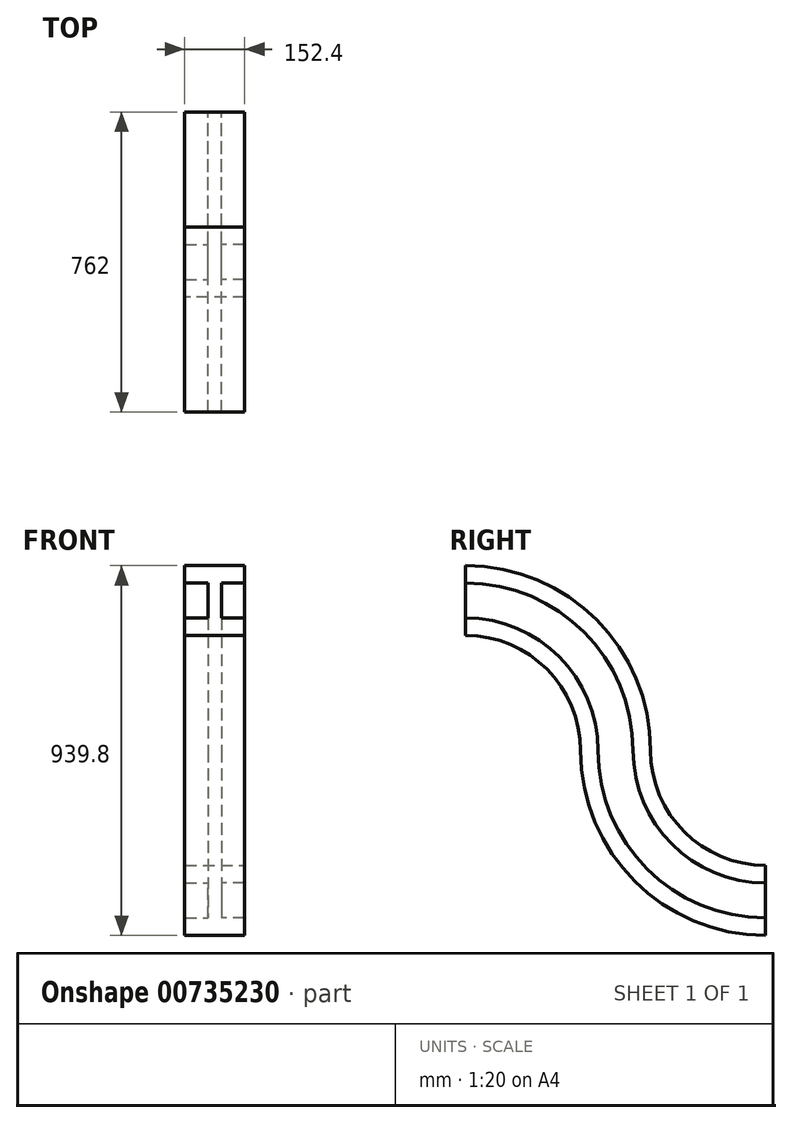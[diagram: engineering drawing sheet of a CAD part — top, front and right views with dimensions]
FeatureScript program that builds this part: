
annotation { "Feature Type Name" : "Feature", "Feature Type Description" : "" }
export const myFeature = defineFeature(function(context is Context, id is Id, definition is map)
    precondition{}
    {
        {
            var Q0;
            Q0=qCreatedBy(makeId("Front.planeOp"),FACE);
            var sketch = newSketch(context, id + "F0", { "sketchPlane" : qUnion([Q0])});
            skLineSegment(sketch, "E0", {"start": v(0, 88.9) * mm, "end": v(76.2, 88.9) * mm});
            skLineSegment(sketch, "E1", {"start": v(76.2, 88.9) * mm, "end": v(76.2, 44.45) * mm});
            skLineSegment(sketch, "E2", {"start": v(76.2, 44.45) * mm, "end": v(17.37, 44.45) * mm});
            skLineSegment(sketch, "E3", {"start": v(0, 88.9) * mm, "end": v(0, -88.9) * mm, "construction": true});
            skLineSegment(sketch, "E4", {"start": v(-17.37, 0) * mm, "end": v(17.37, 0) * mm, "construction": true});
            skLineSegment(sketch, "E5", {"start": v(17.37, 0) * mm, "end": v(17.37, 44.45) * mm});
            skLineSegment(sketch, "E6.MirrorCS", {"start": v(0, 88.9) * mm, "end": v(-76.2, 88.9) * mm});
            skLineSegment(sketch, "E7.MirrorCS", {"start": v(-76.2, 88.9) * mm, "end": v(-76.2, 44.45) * mm});
            skLineSegment(sketch, "E8.MirrorCS", {"start": v(-17.37, 0) * mm, "end": v(-17.37, 44.45) * mm});
            skLineSegment(sketch, "E9.MirrorCS", {"start": v(-76.2, 44.45) * mm, "end": v(-17.37, 44.45) * mm});
            skLineSegment(sketch, "E10.MirrorCS", {"start": v(0, -88.9) * mm, "end": v(-76.2, -88.9) * mm});
            skLineSegment(sketch, "E11.MirrorCS", {"start": v(-76.2, -88.9) * mm, "end": v(-76.2, -44.45) * mm});
            skLineSegment(sketch, "E12.MirrorCS", {"start": v(-76.2, -44.45) * mm, "end": v(-17.37, -44.45) * mm});
            skLineSegment(sketch, "E13.MirrorCS", {"start": v(-17.37, 0) * mm, "end": v(-17.37, -44.45) * mm});
            skLineSegment(sketch, "E14.MirrorCS", {"start": v(76.2, -44.45) * mm, "end": v(17.37, -44.45) * mm});
            skLineSegment(sketch, "E15.MirrorCS", {"start": v(0, -88.9) * mm, "end": v(76.2, -88.9) * mm});
            skLineSegment(sketch, "E16.MirrorCS", {"start": v(17.37, 0) * mm, "end": v(17.37, -44.45) * mm});
            skLineSegment(sketch, "E17.MirrorCS", {"start": v(76.2, -88.9) * mm, "end": v(76.2, -44.45) * mm});
            skSolve(sketch);
        }
        {
            var Q0;
            Q0=qCreatedBy(makeId("Right.planeOp"),FACE);
            var sketch = newSketch(context, id + "F1", { "sketchPlane" : qUnion([Q0])});
            skArc(sketch, "E18", {"start": v(0, 0) * mm, "mid": v(269.4, -111.6) * mm, "end": v(381, -381) * mm});
            skArc(sketch, "E19", {"start": v(381, -381) * mm, "mid": v(492.6, -650.4) * mm, "end": v(762, -762) * mm});
            skSolve(sketch);
        }
        {
            var Q0;
            Q0=makeQuery(id+"F0.imprint","IMPRINT",FACE,{"disambiguationData":[TD([[makeQuery(id+"F0.imprint","IMPRINT",EDGE,{"derivedFrom":sQuery(id+"F0.wireOp",EDGE,"E0")}),-1.0]])]});
            var Q1;
            Q1=sQuery(id+"F1.wireOp",EDGE,"E18");
            sweep(context, id + "F2", {"profiles" : qUnion([Q0]), "path" : qUnion([Q1])});
        }
        {
            var Q0;
            Q0=makeQuery(id+"F2.opSweep","CAP_FACE",FACE,{"disambiguationData":[OSD([sQuery(id+"F0.wireOp",EDGE,"E0"),sQuery(id+"F0.wireOp",EDGE,"E1"),sQuery(id+"F0.wireOp",EDGE,"E2"),sQuery(id+"F0.wireOp",EDGE,"E5"),sQuery(id+"F0.wireOp",EDGE,"E6.MirrorCS"),sQuery(id+"F0.wireOp",EDGE,"E8.MirrorCS"),sQuery(id+"F0.wireOp",EDGE,"E9.MirrorCS"),sQuery(id+"F0.wireOp",EDGE,"E7.MirrorCS"),sQuery(id+"F0.wireOp",EDGE,"E10.MirrorCS"),sQuery(id+"F0.wireOp",EDGE,"E11.MirrorCS"),sQuery(id+"F0.wireOp",EDGE,"E12.MirrorCS"),sQuery(id+"F0.wireOp",EDGE,"E13.MirrorCS"),sQuery(id+"F0.wireOp",EDGE,"E14.MirrorCS"),sQuery(id+"F0.wireOp",EDGE,"E15.MirrorCS"),sQuery(id+"F0.wireOp",EDGE,"E16.MirrorCS"),sQuery(id+"F0.wireOp",EDGE,"E17.MirrorCS"),sQuery(id+"F1.wireOp",VERTEX,"E18.start")])],"isStart":true});
            var Q1;
            Q1 = qBodyType(qCreatedBy(id + "F1" ,EDGE), BodyType.WIRE);
            sweep(context, id + "F3", {"operationType" : NewBodyOperationType.ADD, "profiles" : qUnion([Q0]), "path" : qUnion([Q1])});
        }
        {
            var Q0;
            Q0=makeQuery(id+"F0.imprint","IMPRINT",FACE,{"disambiguationData":[TD([[makeQuery(id+"F0.imprint","IMPRINT",EDGE,{"derivedFrom":sQuery(id+"F0.wireOp",EDGE,"E0")}),-1.0]])]});
            var Q1;
            Q1=sQuery(id+"F1.wireOp",EDGE,"E18");
            var Q2;
            Q2=sQuery(id+"F1.wireOp",EDGE,"E19");
            sweep(context, id + "F4", {"profiles" : qUnion([Q0]), "path" : qUnion([Q1, Q2])});
        }
    });
